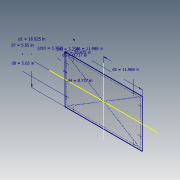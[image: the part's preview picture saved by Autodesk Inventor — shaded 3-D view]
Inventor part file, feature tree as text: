
AUTODESK INVENTOR PART (.ipt)
format: ipt  version: 2020.3 (Build 243373000, 373)  size: 114,176 bytes
history: native  units: in
note: dims shown in document units (in); Inventor stores cm internally (conversion verified against a paired STEP export)
features: sketch x1, extrude x1, hole x1, fillet x1
ambient origin geometry x8: Origin, YZ Plane, XZ Plane, XY Plane, X Axis, Y Axis, Z Axis, Center Point
bodies: Solid1 (feature_tree)
feature tree (4):
  sketch  "Sketch1"  dims[d0=30.475in d1=18.825in d3=0.737in d4=0.737in d5=11.988in d6=11.988in d7=5.65in d8=5.65in d9=3.2495in d10=3.7625in d11=0.177in d12=0.0in d13=0.3125in d14=0.75in d15=0.375in d16=0.25in d17=0.5635in d18=1.0in d19=0.8108in d20=0.25in]
  extrude  "Extrusion1"  Depth=18.825in
  hole  "Hole1"  [1 undecoded]
  fillet  "Fillet1"  Radius=0.737in
note: 1 required parameter value undecoded (feature->parameter linkage not recoverable at this tier; creation-order binding heuristic only, values carry confidence <= 0.55)
